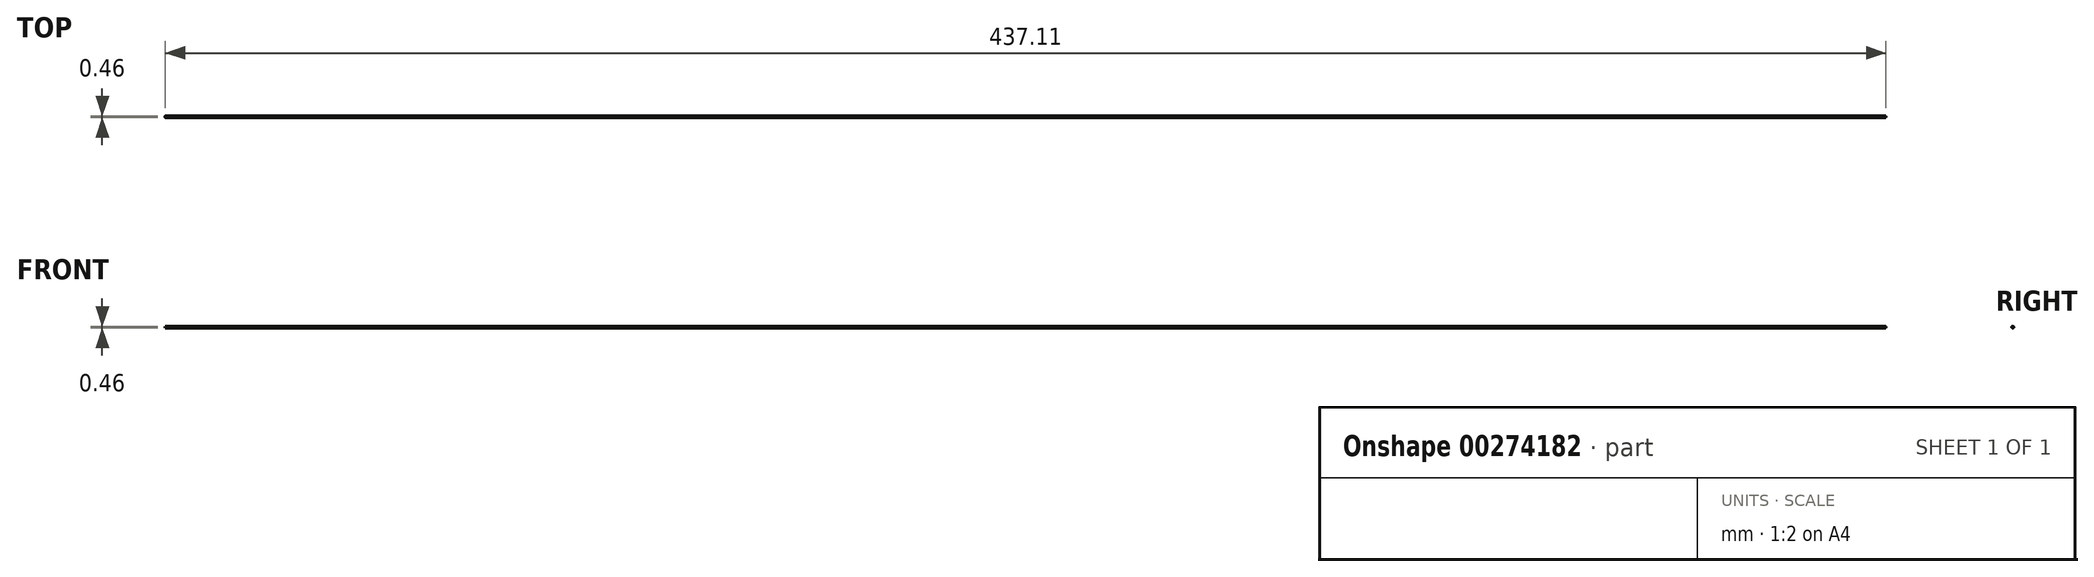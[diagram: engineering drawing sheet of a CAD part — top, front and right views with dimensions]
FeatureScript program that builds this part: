
annotation { "Feature Type Name" : "Feature", "Feature Type Description" : "" }
export const myFeature = defineFeature(function(context is Context, id is Id, definition is map)
    precondition{}
    {
        {
            var Q0;
            Q0=qCreatedBy(makeId("Top.planeOp"),FACE);
            var sketch = newSketch(context, id + "F0", { "sketchPlane" : qUnion([Q0])});
            skArc(sketch, "E0", {"start": v(0, -0.23) * mm, "mid": v(0.23, 0) * mm, "end": v(0, 0.23) * mm});
            skLineSegment(sketch, "E1", {"start": v(0, 0.23) * mm, "end": v(0, -0.23) * mm});
            skSolve(sketch);
        }
        {
            var Q0;
            Q0=makeQuery(id+"F0.imprint","IMPRINT",FACE,{"disambiguationData":[TD([[makeQuery(id+"F0.imprint","IMPRINT",EDGE,{"derivedFrom":sQuery(id+"F0.wireOp",EDGE,"E0")}),1.0]])]});
            var Q1;
            Q1=sQuery(id+"F0.wireOp",EDGE,"E1");
            revolve(context, id + "F1", {"entities" : qUnion([Q0]), "axis" : qUnion([Q1]), "revolveType" : RevolveType.FULL});
        }
        {
            var Q0;
            Q0=qCreatedBy(makeId("Right.planeOp"),FACE);
            var sketch = newSketch(context, id + "F2", { "sketchPlane" : qUnion([Q0])});
            skCircle(sketch, "E2", {"center": v(0, 0) * mm, "radius": 0.23 * mm});
            skSolve(sketch);
        }
        {
            var Q0;
            Q0=makeQuery(id+"F2.imprint","IMPRINT",FACE,{"disambiguationData":[TD([[makeQuery(id+"F2.imprint","IMPRINT",EDGE,{"derivedFrom":sQuery(id+"F2.wireOp",EDGE,"E2")}),1.0]])]});
            extrude(context, id + "F3", {"entities" : qUnion([Q0]), "operationType" : NewBodyOperationType.ADD, "oppositeDirection" : true, "depth" : 436.88 * mm});
        }
    });
